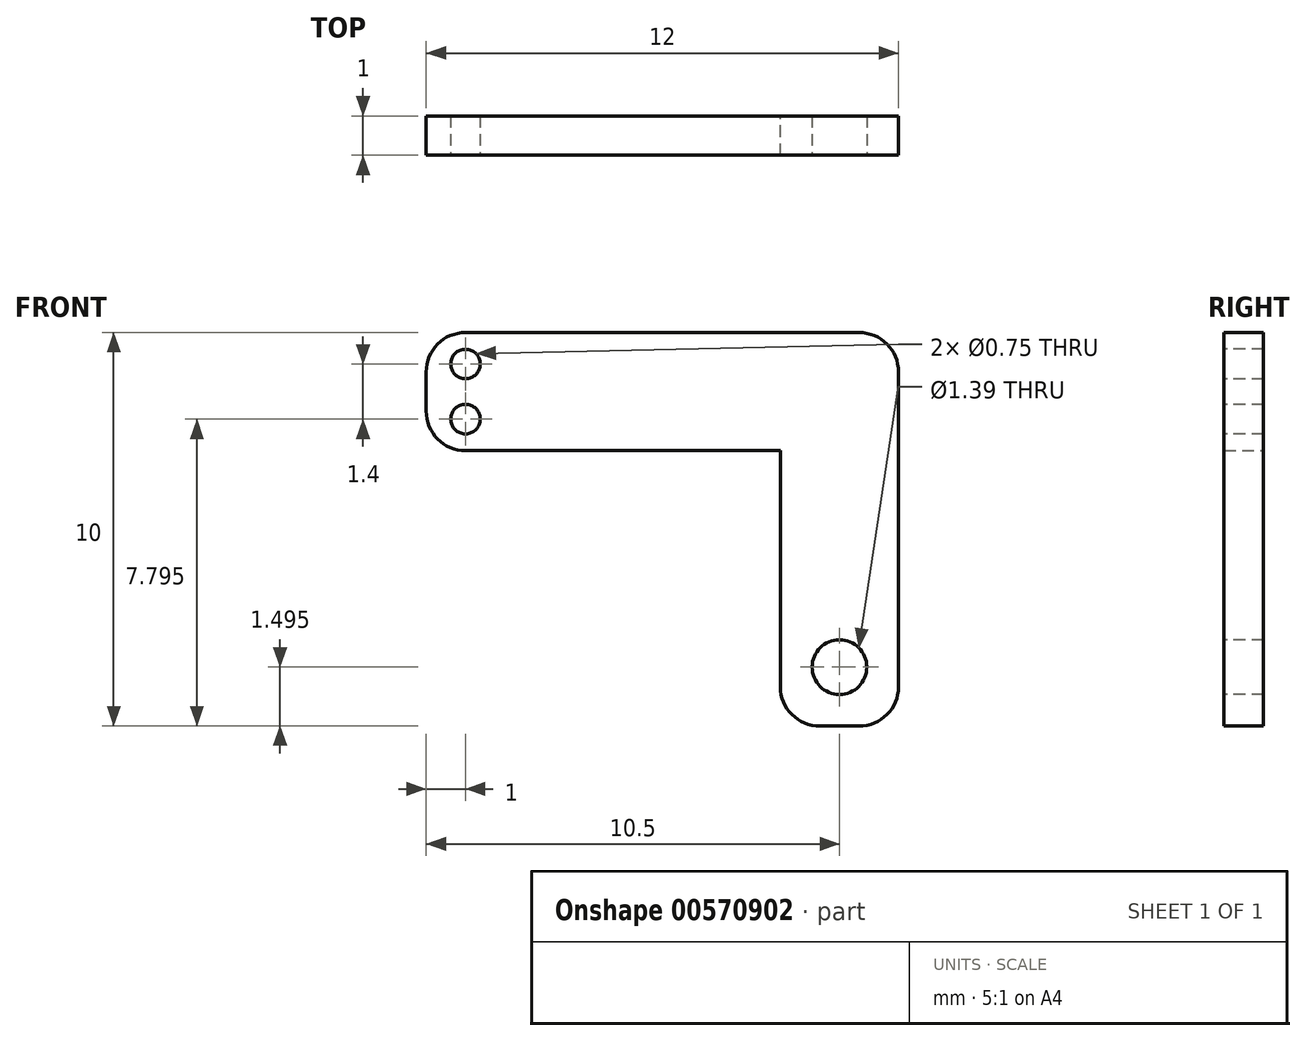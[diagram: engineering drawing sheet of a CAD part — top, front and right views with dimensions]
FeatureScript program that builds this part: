
annotation { "Feature Type Name" : "Feature", "Feature Type Description" : "" }
export const myFeature = defineFeature(function(context is Context, id is Id, definition is map)
    precondition{}
    {
        {
            var Q0;
            Q0=qCreatedBy(makeId("Front.planeOp"),FACE);
            var sketch = newSketch(context, id + "F0", { "sketchPlane" : qUnion([Q0])});
            skLineSegment(sketch, "E0", {"start": v(1, 5.15) * mm, "end": v(9, 5.15) * mm});
            skLineSegment(sketch, "E1", {"start": v(9, 5.15) * mm, "end": v(9, -0.85) * mm});
            skLineSegment(sketch, "E2", {"start": v(10, -1.85) * mm, "end": v(11, -1.85) * mm});
            skLineSegment(sketch, "E3", {"start": v(12, -0.85) * mm, "end": v(12, 7.15) * mm});
            skLineSegment(sketch, "E4", {"start": v(11, 8.15) * mm, "end": v(1, 8.15) * mm});
            skLineSegment(sketch, "E5", {"start": v(0, 7.15) * mm, "end": v(0, 6.15) * mm});
            skPoint(sketch, "E6.visualSharp", {"position": v(12, 8.15) * mm});
            skArc(sketch, "E6.filletArc", {"start": v(12, 7.15) * mm, "mid": v(11.7, 7.85) * mm, "end": v(11, 8.15) * mm});
            skPoint(sketch, "E7.visualSharp", {"position": v(0, 8.15) * mm});
            skArc(sketch, "E7.filletArc", {"start": v(1, 8.15) * mm, "mid": v(0.3, 7.85) * mm, "end": v(0, 7.15) * mm});
            skPoint(sketch, "E8.visualSharp", {"position": v(0, 5.15) * mm});
            skArc(sketch, "E8.filletArc", {"start": v(0, 6.15) * mm, "mid": v(0.3, 5.44) * mm, "end": v(1, 5.15) * mm});
            skPoint(sketch, "E9.visualSharp", {"position": v(9, -1.85) * mm});
            skArc(sketch, "E9.filletArc", {"start": v(9, -0.85) * mm, "mid": v(9.3, -1.56) * mm, "end": v(10, -1.85) * mm});
            skPoint(sketch, "E10.visualSharp", {"position": v(12, -1.85) * mm});
            skArc(sketch, "E10.filletArc", {"start": v(11, -1.85) * mm, "mid": v(11.7, -1.56) * mm, "end": v(12, -0.85) * mm});
            skSolve(sketch);
        }
        {
            var Q0;
            Q0 = qSketchRegion(id + "F0", true);
            extrude(context, id + "F1", {"entities" : qUnion([Q0]), "depth" : 1 * mm, "offsetDistance" : 25 * mm});
        }
        {
            var Q0;
            Q0=makeQuery(id+"F1.opExtrude","CAP_FACE",FACE,{"disambiguationData":[OSD([sQuery(id+"F0.wireOp",EDGE,"E0"),sQuery(id+"F0.wireOp",EDGE,"E1"),sQuery(id+"F0.wireOp",EDGE,"E2"),sQuery(id+"F0.wireOp",EDGE,"E3"),sQuery(id+"F0.wireOp",EDGE,"E4"),sQuery(id+"F0.wireOp",EDGE,"E5")])],"isStart":false});
            var sketch = newSketch(context, id + "F2", { "sketchPlane" : qUnion([Q0])});
            skSolve(sketch);
        }
        {
            var Q0;
            Q0=makeQuery(id+"F2.imprint","IMPRINT",FACE,{"disambiguationData":[TD([[makeQuery(id+"F2.imprint","IMPRINT",EDGE,{"derivedFrom":makeQuery(id+"F1.opExtrude","CAP_EDGE",EDGE,{"disambiguationData":[OSD([sQuery(id+"F0.wireOp",EDGE,"E0")])],"isStart":false})}),1.0]])]});
            var sketch = newSketch(context, id + "F3", { "sketchPlane" : qUnion([Q0])});
            skCircle(sketch, "E11", {"center": v(1, 7.35) * mm, "radius": 0.38 * mm});
            skCircle(sketch, "E12", {"center": v(1, 5.95) * mm, "radius": 0.38 * mm});
            skCircle(sketch, "E13", {"center": v(10.5, -0.35) * mm, "radius": 0.7 * mm});
            skSolve(sketch);
        }
        {
            var Q0;
            Q0 = qSketchRegion(id + "F3", true);
            extrude(context, id + "F4", {"entities" : qUnion([Q0]), "operationType" : NewBodyOperationType.REMOVE, "oppositeDirection" : true, "depth" : 25 * mm, "offsetDistance" : 25 * mm});
        }
    });
